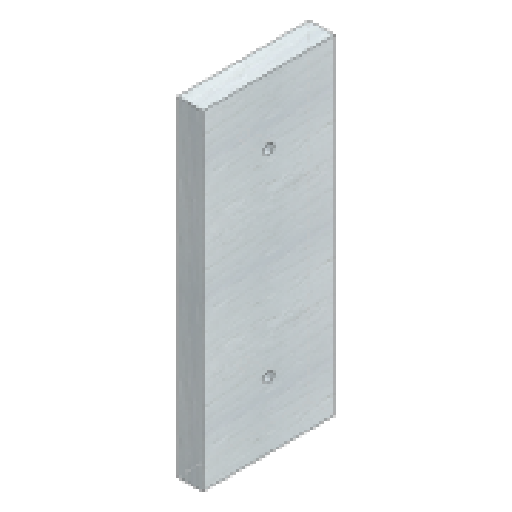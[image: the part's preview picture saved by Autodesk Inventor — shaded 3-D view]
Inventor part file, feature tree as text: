
AUTODESK INVENTOR PART (.ipt)
format: ipt  version: 2024 (Build 280153000, 153)  size: 108,032 bytes
history: native  units: in
note: dims shown in document units (in); Inventor stores cm internally (conversion verified against a paired STEP export)
features: extrude x1, sketch x1
ambient origin geometry x8: Origin, YZ Plane, XZ Plane, XY Plane, X Axis, Y Axis, Z Axis, Center Point
bodies: Solid1 (feature_tree)
feature tree (2):
  extrude  "Extrusion1"  Depth=3.937in
  sketch  "Sketch1"  dims[d0=9.8425in d1=3.937in d2=1.9685in d3=1.9685in d4=0.315in d5=0.315in d6=0.748in d7=0.0in]
